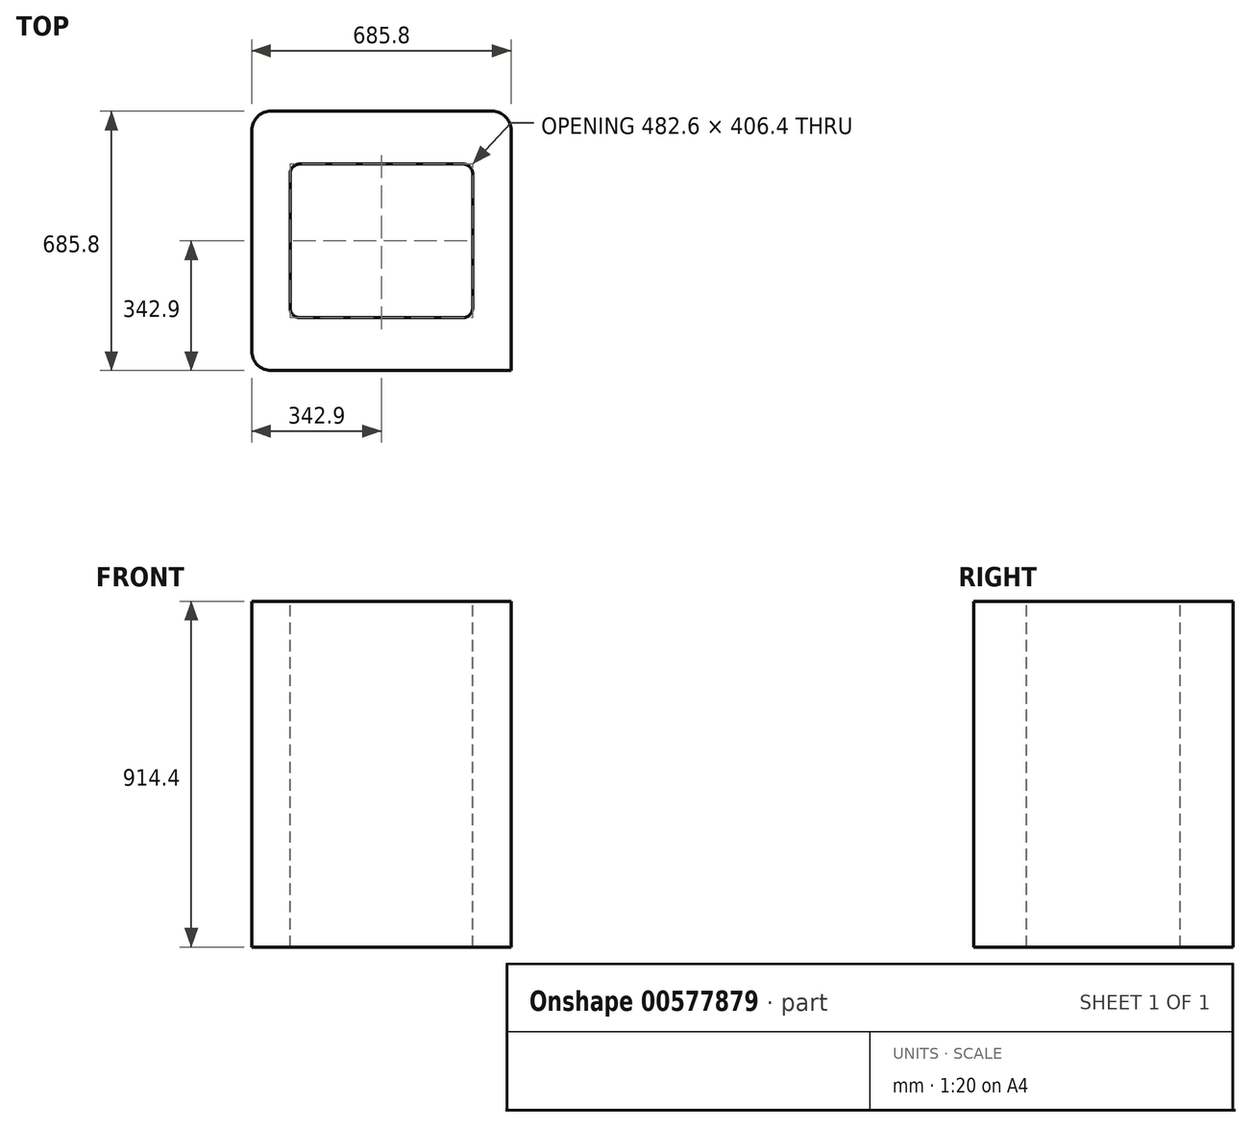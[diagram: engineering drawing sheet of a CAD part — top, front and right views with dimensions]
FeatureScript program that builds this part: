
annotation { "Feature Type Name" : "Feature", "Feature Type Description" : "" }
export const myFeature = defineFeature(function(context is Context, id is Id, definition is map)
    precondition{}
    {
        {
            var Q0;
            Q0=qCreatedBy(makeId("Top.planeOp"),FACE);
            var sketch = newSketch(context, id + "F0", { "sketchPlane" : qUnion([Q0])});
            skLineSegment(sketch, "E0.bottom", {"start": v(-292.1, -342.9) * mm, "end": v(342.9, -342.9) * mm});
            skLineSegment(sketch, "E0.top", {"start": v(-292.1, 342.9) * mm, "end": v(292.1, 342.9) * mm});
            skLineSegment(sketch, "E0.left", {"start": v(-342.9, -292.1) * mm, "end": v(-342.9, 292.1) * mm});
            skLineSegment(sketch, "E0.right", {"start": v(342.9, -342.9) * mm, "end": v(342.9, 292.1) * mm});
            skPoint(sketch, "E0.middle", {"position": v(0, 0) * mm});
            skLineSegment(sketch, "E1.bottom", {"start": v(215.9, -203.2) * mm, "end": v(-215.9, -203.2) * mm});
            skLineSegment(sketch, "E1.top", {"start": v(215.9, 203.2) * mm, "end": v(-215.9, 203.2) * mm});
            skLineSegment(sketch, "E1.left", {"start": v(241.3, -177.8) * mm, "end": v(241.3, 177.8) * mm});
            skLineSegment(sketch, "E1.right", {"start": v(-241.3, -177.8) * mm, "end": v(-241.3, 177.8) * mm});
            skPoint(sketch, "E2.visualSharp", {"position": v(-241.3, 203.2) * mm});
            skArc(sketch, "E2.filletArc", {"start": v(-215.9, 203.2) * mm, "mid": v(-233.86, 195.76) * mm, "end": v(-241.3, 177.8) * mm});
            skPoint(sketch, "E3.visualSharp", {"position": v(241.3, 203.2) * mm});
            skArc(sketch, "E3.filletArc", {"start": v(241.3, 177.8) * mm, "mid": v(233.86, 195.76) * mm, "end": v(215.9, 203.2) * mm});
            skPoint(sketch, "E4.visualSharp", {"position": v(241.3, -203.2) * mm});
            skArc(sketch, "E4.filletArc", {"start": v(215.9, -203.2) * mm, "mid": v(233.86, -195.76) * mm, "end": v(241.3, -177.8) * mm});
            skPoint(sketch, "E5.visualSharp", {"position": v(-241.3, -203.2) * mm});
            skArc(sketch, "E5.filletArc", {"start": v(-241.3, -177.8) * mm, "mid": v(-233.86, -195.76) * mm, "end": v(-215.9, -203.2) * mm});
            skLineSegment(sketch, "E6.0", {"start": v(247.65, -177.8) * mm, "end": v(247.65, 177.8) * mm});
            skLineSegment(sketch, "E7.0", {"start": v(215.9, 209.55) * mm, "end": v(-215.9, 209.55) * mm});
            skArc(sketch, "E8.0", {"start": v(247.65, 177.8) * mm, "mid": v(238.35, 200.25) * mm, "end": v(215.9, 209.55) * mm});
            skArc(sketch, "E9.0", {"start": v(-215.9, 209.55) * mm, "mid": v(-238.35, 200.25) * mm, "end": v(-247.65, 177.8) * mm});
            skLineSegment(sketch, "E10.0", {"start": v(-247.65, -177.8) * mm, "end": v(-247.65, 177.8) * mm});
            skArc(sketch, "E11.0", {"start": v(-247.65, -177.8) * mm, "mid": v(-238.35, -200.25) * mm, "end": v(-215.9, -209.55) * mm});
            skLineSegment(sketch, "E12.0", {"start": v(215.9, -209.55) * mm, "end": v(-215.9, -209.55) * mm});
            skArc(sketch, "E13.0", {"start": v(215.9, -205.1) * mm, "mid": v(235.2, -197.1) * mm, "end": v(243.2, -177.8) * mm});
            skPoint(sketch, "E14.visualSharp", {"position": v(-342.9, -342.9) * mm});
            skArc(sketch, "E14.filletArc", {"start": v(-342.9, -292.1) * mm, "mid": v(-328.02, -328.02) * mm, "end": v(-292.1, -342.9) * mm});
            skPoint(sketch, "E15.visualSharp", {"position": v(-342.9, 342.9) * mm});
            skArc(sketch, "E15.filletArc", {"start": v(-292.1, 342.9) * mm, "mid": v(-328.02, 328.02) * mm, "end": v(-342.9, 292.1) * mm});
            skPoint(sketch, "E16.visualSharp", {"position": v(342.9, 342.9) * mm});
            skArc(sketch, "E16.filletArc", {"start": v(342.9, 292.1) * mm, "mid": v(328.02, 328.02) * mm, "end": v(292.1, 342.9) * mm});
            skPoint(sketch, "E17.visualSharp", {"position": v(342.9, -342.9) * mm});
            skSolve(sketch);
        }
        {
            var Q0;
            Q0=makeQuery(id+"F0.imprint","IMPRINT",FACE,{"disambiguationData":[TD([[makeQuery(id+"F0.imprint","IMPRINT",EDGE,{"derivedFrom":sQuery(id+"F0.wireOp",EDGE,"E0.bottom")}),1.0]])]});
            extrude(context, id + "F1", {"entities" : qUnion([Q0]), "oppositeDirection" : true, "depth" : 914.4 * mm, "offsetDistance" : 25.4 * mm});
        }
    });
